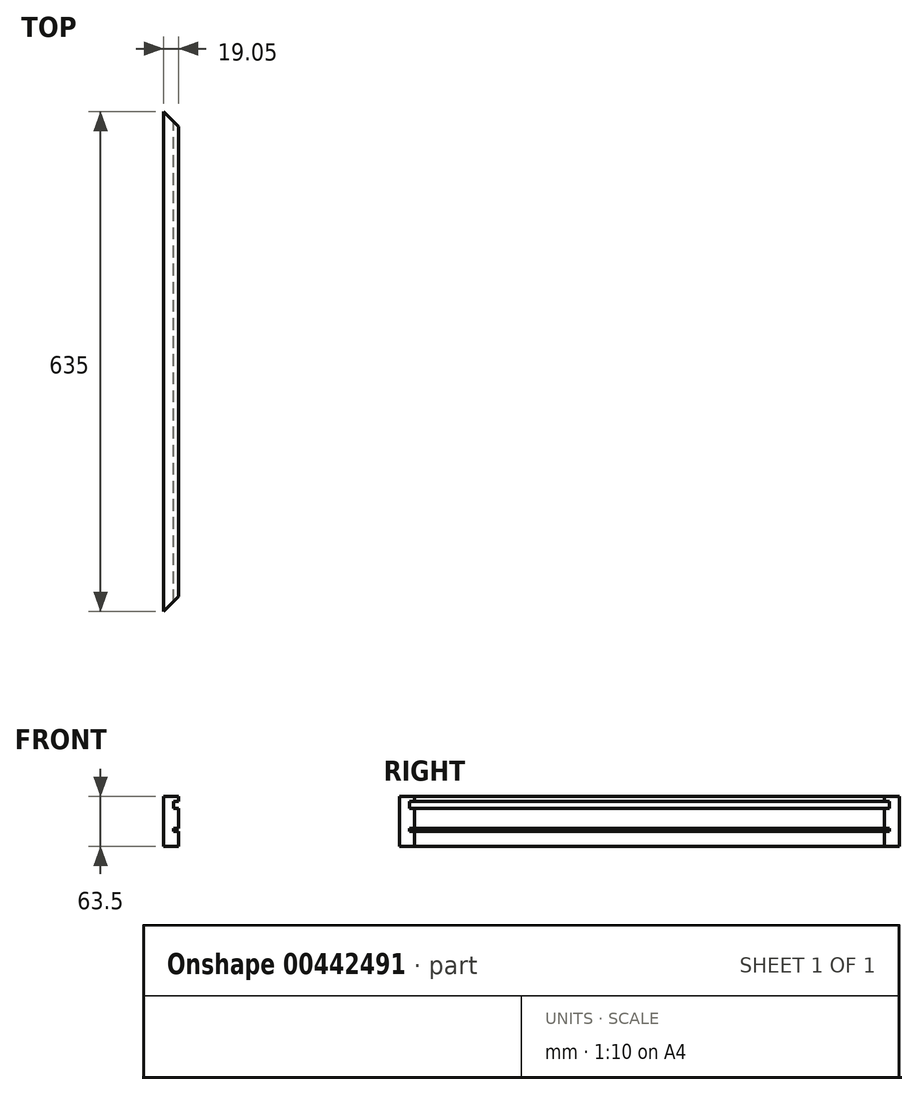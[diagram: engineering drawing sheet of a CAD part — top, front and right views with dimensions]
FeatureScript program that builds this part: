
annotation { "Feature Type Name" : "Feature", "Feature Type Description" : "" }
export const myFeature = defineFeature(function(context is Context, id is Id, definition is map)
    precondition{}
    {
        {
            var Q0;
            Q0=qCreatedBy(makeId("Front.planeOp"),FACE);
            var sketch = newSketch(context, id + "F0", { "sketchPlane" : qUnion([Q0])});
            skLineSegment(sketch, "E0", {"start": v(0, 63.5) * mm, "end": v(19.05, 63.5) * mm});
            skLineSegment(sketch, "E1", {"start": v(19.05, 63.5) * mm, "end": v(19.05, 57.15) * mm});
            skLineSegment(sketch, "E2", {"start": v(19.05, 57.15) * mm, "end": v(12.7, 57.15) * mm});
            skLineSegment(sketch, "E3", {"start": v(12.7, 57.15) * mm, "end": v(12.7, 48.51) * mm});
            skLineSegment(sketch, "E4", {"start": v(12.7, 48.51) * mm, "end": v(19.05, 48.51) * mm});
            skLineSegment(sketch, "E5", {"start": v(19.05, 48.51) * mm, "end": v(19.05, 23.11) * mm});
            skLineSegment(sketch, "E6", {"start": v(19.05, 23.11) * mm, "end": v(12.7, 23.11) * mm});
            skLineSegment(sketch, "E7", {"start": v(12.7, 23.11) * mm, "end": v(12.7, 19.05) * mm});
            skLineSegment(sketch, "E8", {"start": v(12.7, 19.05) * mm, "end": v(19.05, 19.05) * mm});
            skLineSegment(sketch, "E9", {"start": v(0, 0) * mm, "end": v(0, 63.5) * mm});
            skLineSegment(sketch, "E10", {"start": v(0, 0) * mm, "end": v(19.05, 0) * mm});
            skLineSegment(sketch, "E11", {"start": v(19.05, 0) * mm, "end": v(19.05, 19.05) * mm});
            skSolve(sketch);
        }
        {
            var Q0;
            Q0=makeQuery(id+"F0.imprint","IMPRINT",FACE,{"disambiguationData":[TD([[makeQuery(id+"F0.imprint","IMPRINT",EDGE,{"derivedFrom":sQuery(id+"F0.wireOp",EDGE,"E0")}),-1.0]])]});
            extrude(context, id + "F1", {"entities" : qUnion([Q0]), "depth" : 635 * mm});
        }
        {
            var Q0;
            Q0=makeQuery(id+"F1.opExtrude","SWEPT_FACE",FACE,{"disambiguationData":[OSD([sQuery(id+"F0.wireOp",EDGE,"E0")])]});
            var sketch = newSketch(context, id + "F2", { "sketchPlane" : qUnion([Q0])});
            skLineSegment(sketch, "E12", {"start": v(0, 0) * mm, "end": v(19.05, 0) * mm});
            skLineSegment(sketch, "E13", {"start": v(19.05, 0) * mm, "end": v(19.05, -19.05) * mm});
            skLineSegment(sketch, "E14", {"start": v(19.05, -19.05) * mm, "end": v(0, 0) * mm});
            skLineSegment(sketch, "E15", {"start": v(0, -635) * mm, "end": v(19.05, -635) * mm});
            skLineSegment(sketch, "E16", {"start": v(19.05, -635) * mm, "end": v(19.05, -615.95) * mm});
            skLineSegment(sketch, "E17", {"start": v(19.05, -615.95) * mm, "end": v(0, -635) * mm});
            skSolve(sketch);
        }
        {
            var Q0;
            Q0=makeQuery(id+"F2.imprint","IMPRINT",FACE,{"disambiguationData":[TD([[makeQuery(id+"F2.imprint","IMPRINT",EDGE,{"derivedFrom":sQuery(id+"F2.wireOp",EDGE,"E12")}),-1.0]])]});
            var Q1;
            Q1=makeQuery(id+"F2.imprint","IMPRINT",FACE,{"disambiguationData":[TD([[makeQuery(id+"F2.imprint","IMPRINT",EDGE,{"derivedFrom":sQuery(id+"F2.wireOp",EDGE,"E15")}),1.0]])]});
            extrude(context, id + "F3", {"entities" : qUnion([Q0, Q1]), "operationType" : NewBodyOperationType.REMOVE, "oppositeDirection" : true, "depth" : 63.5 * mm});
        }
    });
